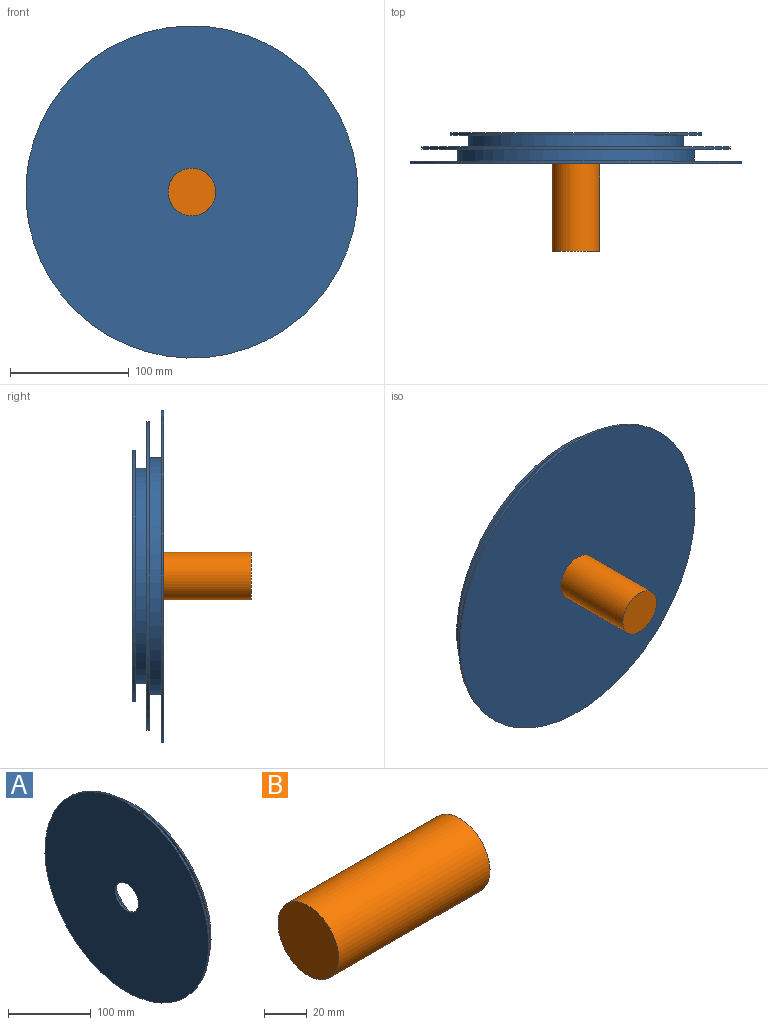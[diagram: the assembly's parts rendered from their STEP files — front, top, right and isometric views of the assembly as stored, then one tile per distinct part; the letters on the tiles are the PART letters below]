
ASSEMBLY  parts=2 mates=1
PART A: 20 faces, bbox 26x279.9x279.9 mm
  f0: plane 279.91x279.91mm, normal (-1,0,0), area 60277.2mm2, adj f1,f19
  f1: cylinder r=20mm len=40mm, axis (-1,0,0), area 251.3mm2, adj f0,f2
  f2: plane 120x120mm, normal (1,0,0), area 10053.1mm2, adj f1,f3
  f3: cylinder r=60mm len=120mm, axis (-1,0,0), area 3769.9mm2, adj f2,f4
  f4: plane 120x120mm, normal (-1,0,0), area 6920mm2, adj f3,f5
  f5: cylinder r=37.38mm len=74.76mm, axis (-1,0,0), area 469.7mm2, adj f4,f6
  f6: plane 137.23x137.23mm, normal (1,0,0), area 10399.8mm2, adj f5,f7
  f7: cylinder r=68.61mm len=137.23mm, axis (-1,0,0), area 4311mm2, adj f6,f8
  f8: plane 137.23x137.23mm, normal (-1,0,0), area 7041.8mm2, adj f7,f9
  f9: cylinder r=49.66mm len=99.32mm, axis (-1,0,0), area 624.1mm2, adj f8,f10
  f10: plane 212.42x212.42mm, normal (1,0,0), area 27692.2mm2, adj f9,f11
  f11: cylinder r=106.21mm len=212.42mm, axis (-1,0,0), area 1334.7mm2, adj f10,f12
  f12: plane 212.42x212.42mm, normal (-1,0,0), area 9460.8mm2, adj f11,f13
  f13: cylinder r=90.94mm len=181.87mm, axis (-1,0,0), area 5713.7mm2, adj f12,f14
  f14: plane 259.91x259.91mm, normal (1,0,0), area 27075.4mm2, adj f13,f15
  f15: cylinder r=129.95mm len=259.91mm, axis (-1,0,0), area 1633mm2, adj f14,f16
  f16: plane 259.91x259.91mm, normal (-1,0,0), area 21668.1mm2, adj f15,f17
  f17: cylinder r=99.95mm len=199.91mm, axis (-1,0,0), area 6280.2mm2, adj f16,f18
  f18: plane 279.91x279.91mm, normal (1,0,0), area 30147.5mm2, adj f17,f19
  f19: cylinder r=139.95mm len=279.91mm, axis (-1,0,0), area 1758.7mm2, adj f0,f18
PART B: 3 faces, bbox 100x40x40 mm
  f0: cylinder r=20mm len=100mm, axis (-1,0,0), area 12566.4mm2, adj f1,f2
  f1: plane 40x40mm, normal (1,0,0), area 1256.6mm2, adj f0
  f2: plane 40x40mm, normal (-1,0,0), area 1256.6mm2, adj f0
PLACE A rot(axis=(0.58,0.58,0.58),120deg) t=(-5.79,-60.28,93.1)mm
PLACE B rot(axis=(0,0,-1),90deg) t=(310.25,-64.49,38.9)mm
MATE slider A.f1 <-> B.f0  axis (0,1,0) through (-5.79,-88.49,9.24)mm
